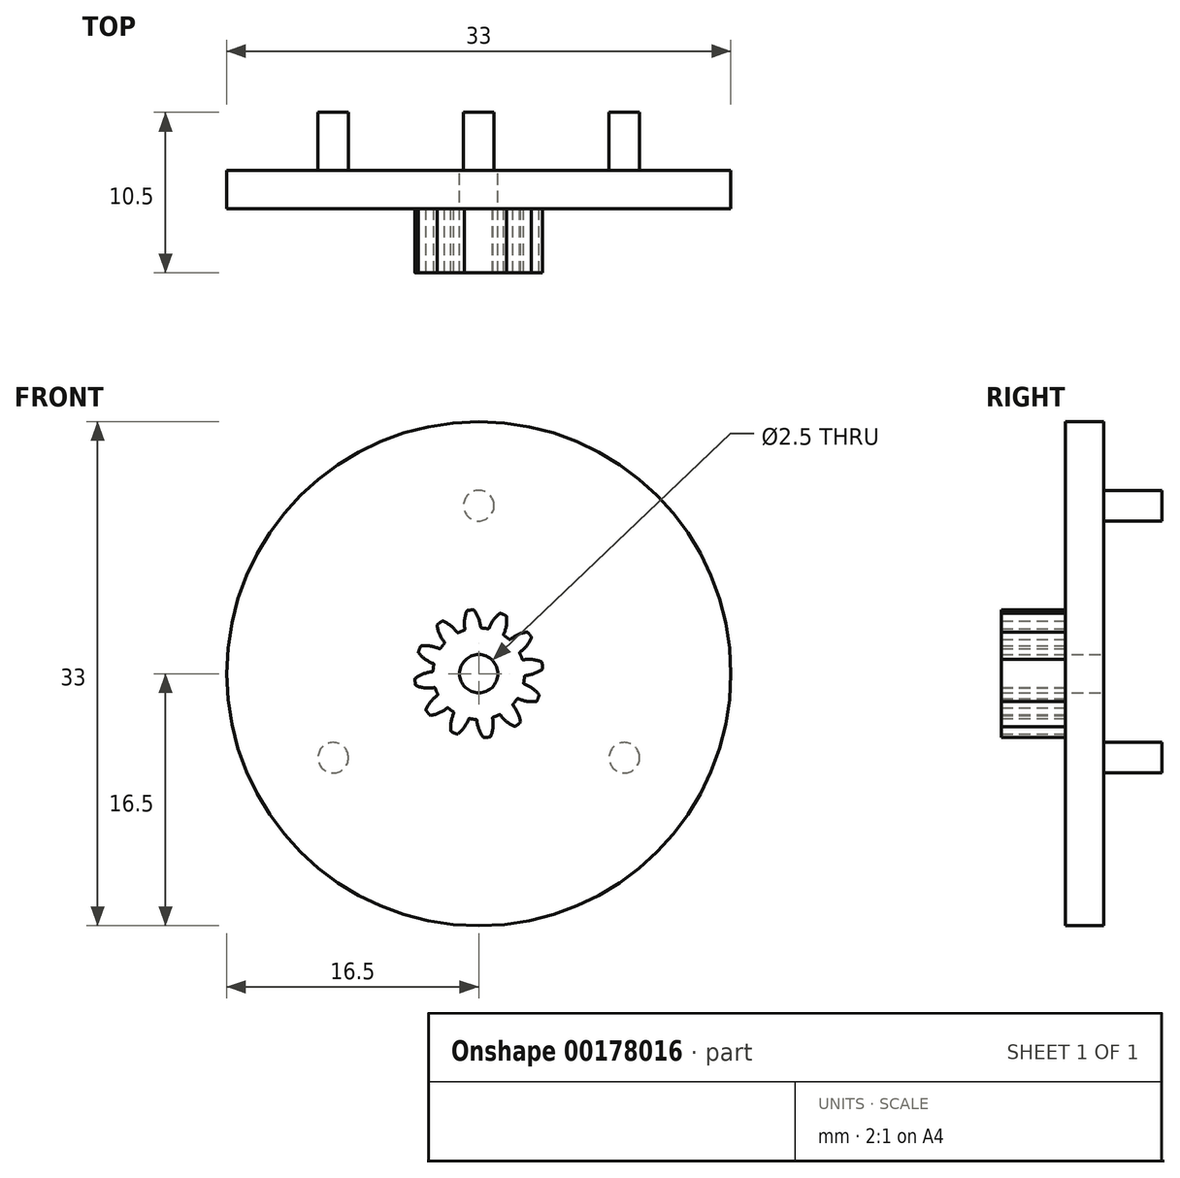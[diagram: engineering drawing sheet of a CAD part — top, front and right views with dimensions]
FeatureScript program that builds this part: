
annotation { "Feature Type Name" : "Feature", "Feature Type Description" : "" }
export const myFeature = defineFeature(function(context is Context, id is Id, definition is map)
    precondition{}
    {
        {
            var Q0;
            Q0=qCreatedBy(makeId("Front.planeOp"),FACE);
            var sketch = newSketch(context, id + "F0", { "sketchPlane" : qUnion([Q0])});
            skCircle(sketch, "E0", {"center": v(0, 0) * mm, "radius": 4.2 * mm, "construction": true});
            skCircle(sketch, "E1", {"center": v(0, 0) * mm, "radius": 3.6 * mm, "construction": true});
            skCircle(sketch, "E2", {"center": v(0, 0) * mm, "radius": 3 * mm, "construction": true});
            skLineSegment(sketch, "E3", {"start": v(0, 0) * mm, "end": v(0, 0.84) * mm, "construction": true});
            skLineSegment(sketch, "E4", {"start": v(0, 3.6) * mm, "end": v(-6.08, 3.6) * mm, "construction": true});
            skLineSegment(sketch, "E5", {"start": v(0, 3.6) * mm, "end": v(-6.1, 1.38) * mm, "construction": true});
            skCircle(sketch, "E6", {"center": v(0, 3.6) * mm, "radius": 2.16 * mm, "construction": true});
            skCircle(sketch, "E7", {"center": v(-2.03, 2.86) * mm, "radius": 2.16 * mm, "construction": true});
            skArc(sketch, "E8", {"start": v(-0.3, 4.16) * mm, "mid": v(-0.01, 3.64) * mm, "end": v(0.12, 3.06) * mm});
            skPoint(sketch, "E9.0.midPoint", {"position": v(-1.28, 0.84) * mm});
            skCircle(sketch, "E10.cCircle", {"center": v(0, 0) * mm, "radius": 0.84 * mm, "construction": true});
            skLineSegment(sketch, "E10.0", {"start": v(0, 0.84) * mm, "end": v(0.1, 0.83) * mm, "construction": true});
            skLineSegment(sketch, "E10.1", {"start": v(0.1, 0.83) * mm, "end": v(0.22, 0.8) * mm, "construction": true});
            skLineSegment(sketch, "E10.2", {"start": v(0.22, 0.8) * mm, "end": v(0.32, 0.77) * mm, "construction": true});
            skLineSegment(sketch, "E10.3", {"start": v(0.32, 0.77) * mm, "end": v(0.42, 0.72) * mm, "construction": true});
            skLineSegment(sketch, "E10.4", {"start": v(0.42, 0.72) * mm, "end": v(0.5, 0.66) * mm, "construction": true});
            skLineSegment(sketch, "E10.5", {"start": v(0.5, 0.66) * mm, "end": v(0.6, 0.6) * mm, "construction": true});
            skLineSegment(sketch, "E10.6", {"start": v(0.6, 0.6) * mm, "end": v(0.66, 0.5) * mm, "construction": true});
            skLineSegment(sketch, "E10.7", {"start": v(0.66, 0.5) * mm, "end": v(0.72, 0.42) * mm, "construction": true});
            skLineSegment(sketch, "E10.8", {"start": v(0.72, 0.42) * mm, "end": v(0.77, 0.32) * mm, "construction": true});
            skLineSegment(sketch, "E10.9", {"start": v(0.77, 0.32) * mm, "end": v(0.8, 0.22) * mm, "construction": true});
            skLineSegment(sketch, "E10.10", {"start": v(0.8, 0.22) * mm, "end": v(0.83, 0.1) * mm, "construction": true});
            skLineSegment(sketch, "E10.11", {"start": v(0.83, 0.1) * mm, "end": v(0.84, 0) * mm, "construction": true});
            skLineSegment(sketch, "E10.12", {"start": v(0.84, 0) * mm, "end": v(0.83, -0.1) * mm, "construction": true});
            skLineSegment(sketch, "E10.13", {"start": v(0.83, -0.1) * mm, "end": v(0.8, -0.22) * mm, "construction": true});
            skLineSegment(sketch, "E10.14", {"start": v(0.8, -0.22) * mm, "end": v(0.77, -0.32) * mm, "construction": true});
            skLineSegment(sketch, "E10.15", {"start": v(0.77, -0.32) * mm, "end": v(0.72, -0.42) * mm, "construction": true});
            skLineSegment(sketch, "E10.16", {"start": v(0.72, -0.42) * mm, "end": v(0.66, -0.5) * mm, "construction": true});
            skLineSegment(sketch, "E10.17", {"start": v(0.66, -0.5) * mm, "end": v(0.6, -0.6) * mm, "construction": true});
            skLineSegment(sketch, "E10.18", {"start": v(0.6, -0.6) * mm, "end": v(0.5, -0.66) * mm, "construction": true});
            skLineSegment(sketch, "E10.19", {"start": v(0.5, -0.66) * mm, "end": v(0.42, -0.72) * mm, "construction": true});
            skLineSegment(sketch, "E10.20", {"start": v(0.42, -0.72) * mm, "end": v(0.32, -0.77) * mm, "construction": true});
            skLineSegment(sketch, "E10.21", {"start": v(0.32, -0.77) * mm, "end": v(0.22, -0.8) * mm, "construction": true});
            skLineSegment(sketch, "E10.22", {"start": v(0.22, -0.8) * mm, "end": v(0.1, -0.83) * mm, "construction": true});
            skLineSegment(sketch, "E10.23", {"start": v(0.1, -0.83) * mm, "end": v(0, -0.84) * mm, "construction": true});
            skLineSegment(sketch, "E10.24", {"start": v(0, -0.84) * mm, "end": v(-0.1, -0.83) * mm, "construction": true});
            skLineSegment(sketch, "E10.25", {"start": v(-0.1, -0.83) * mm, "end": v(-0.22, -0.8) * mm, "construction": true});
            skLineSegment(sketch, "E10.26", {"start": v(-0.22, -0.8) * mm, "end": v(-0.32, -0.77) * mm, "construction": true});
            skLineSegment(sketch, "E10.27", {"start": v(-0.32, -0.77) * mm, "end": v(-0.42, -0.72) * mm, "construction": true});
            skLineSegment(sketch, "E10.28", {"start": v(-0.42, -0.72) * mm, "end": v(-0.5, -0.66) * mm, "construction": true});
            skLineSegment(sketch, "E10.29", {"start": v(-0.5, -0.66) * mm, "end": v(-0.6, -0.6) * mm, "construction": true});
            skLineSegment(sketch, "E10.30", {"start": v(-0.6, -0.6) * mm, "end": v(-0.66, -0.5) * mm, "construction": true});
            skLineSegment(sketch, "E10.31", {"start": v(-0.66, -0.5) * mm, "end": v(-0.72, -0.42) * mm, "construction": true});
            skLineSegment(sketch, "E10.32", {"start": v(-0.72, -0.42) * mm, "end": v(-0.77, -0.32) * mm, "construction": true});
            skLineSegment(sketch, "E10.33", {"start": v(-0.77, -0.32) * mm, "end": v(-0.8, -0.22) * mm, "construction": true});
            skLineSegment(sketch, "E10.34", {"start": v(-0.8, -0.22) * mm, "end": v(-0.83, -0.1) * mm, "construction": true});
            skLineSegment(sketch, "E10.35", {"start": v(-0.83, -0.1) * mm, "end": v(-0.84, 0) * mm, "construction": true});
            skLineSegment(sketch, "E10.36", {"start": v(-0.84, 0) * mm, "end": v(-0.83, 0.1) * mm, "construction": true});
            skLineSegment(sketch, "E10.37", {"start": v(-0.83, 0.1) * mm, "end": v(-0.8, 0.22) * mm, "construction": true});
            skLineSegment(sketch, "E10.38", {"start": v(-0.8, 0.22) * mm, "end": v(-0.77, 0.32) * mm, "construction": true});
            skLineSegment(sketch, "E10.39", {"start": v(-0.77, 0.32) * mm, "end": v(-0.72, 0.42) * mm, "construction": true});
            skLineSegment(sketch, "E10.40", {"start": v(-0.72, 0.42) * mm, "end": v(-0.66, 0.5) * mm, "construction": true});
            skLineSegment(sketch, "E10.41", {"start": v(-0.66, 0.5) * mm, "end": v(-0.6, 0.6) * mm, "construction": true});
            skLineSegment(sketch, "E10.42", {"start": v(-0.6, 0.6) * mm, "end": v(-0.5, 0.66) * mm, "construction": true});
            skLineSegment(sketch, "E10.43", {"start": v(-0.5, 0.66) * mm, "end": v(-0.42, 0.72) * mm, "construction": true});
            skLineSegment(sketch, "E10.44", {"start": v(-0.42, 0.72) * mm, "end": v(-0.32, 0.77) * mm, "construction": true});
            skLineSegment(sketch, "E10.45", {"start": v(-0.32, 0.77) * mm, "end": v(-0.22, 0.8) * mm, "construction": true});
            skLineSegment(sketch, "E10.46", {"start": v(-0.22, 0.8) * mm, "end": v(-0.1, 0.83) * mm, "construction": true});
            skLineSegment(sketch, "E10.47", {"start": v(-0.1, 0.83) * mm, "end": v(0, 0.84) * mm, "construction": true});
            skLineSegment(sketch, "E11", {"start": v(0, 0) * mm, "end": v(-0.1, 0.83) * mm, "construction": true});
            skArc(sketch, "E12.MirrorCS", {"start": v(-0.79, 4.1) * mm, "mid": v(-0.93, 3.52) * mm, "end": v(-0.9, 2.92) * mm});
            skArc(sketch, "E13", {"start": v(-0.73, 4.14) * mm, "mid": v(-0.55, 4.16) * mm, "end": v(-0.36, 4.18) * mm});
            skArc(sketch, "E14", {"start": v(-0.96, 2.84) * mm, "mid": v(0.4, -2.97) * mm, "end": v(0.19, 3) * mm});
            skPoint(sketch, "E15.visualSharp", {"position": v(-0.9, 2.86) * mm});
            skArc(sketch, "E15.filletArc", {"start": v(-0.96, 2.84) * mm, "mid": v(-0.92, 2.87) * mm, "end": v(-0.9, 2.92) * mm});
            skPoint(sketch, "E16.visualSharp", {"position": v(-0.77, 4.13) * mm});
            skArc(sketch, "E16.filletArc", {"start": v(-0.73, 4.14) * mm, "mid": v(-0.76, 4.12) * mm, "end": v(-0.79, 4.1) * mm});
            skPoint(sketch, "E17.visualSharp", {"position": v(-0.32, 4.19) * mm});
            skArc(sketch, "E17.filletArc", {"start": v(-0.3, 4.16) * mm, "mid": v(-0.33, 4.18) * mm, "end": v(-0.36, 4.18) * mm});
            skArc(sketch, "E18.filletArc", {"start": v(0.12, 3.06) * mm, "mid": v(0.14, 3.01) * mm, "end": v(0.19, 3) * mm});
            skArc(sketch, "E19.1.0", {"start": v(-2.25, 1.98) * mm, "mid": v(-2.23, 2.03) * mm, "end": v(-2.25, 2.08) * mm});
            skArc(sketch, "E19.1.1", {"start": v(-2.73, 3.15) * mm, "mid": v(-2.56, 2.58) * mm, "end": v(-2.25, 2.08) * mm});
            skArc(sketch, "E19.1.2", {"start": v(-2.7, 3.22) * mm, "mid": v(-2.72, 3.19) * mm, "end": v(-2.73, 3.15) * mm});
            skArc(sketch, "E19.1.3", {"start": v(-2.7, 3.22) * mm, "mid": v(-2.56, 3.33) * mm, "end": v(-2.4, 3.44) * mm});
            skArc(sketch, "E19.1.4", {"start": v(-2.34, 3.45) * mm, "mid": v(-2.37, 3.45) * mm, "end": v(-2.4, 3.44) * mm});
            skArc(sketch, "E19.1.5", {"start": v(-2.34, 3.45) * mm, "mid": v(-1.83, 3.14) * mm, "end": v(-1.42, 2.71) * mm});
            skArc(sketch, "E19.1.6", {"start": v(-1.42, 2.71) * mm, "mid": v(-1.38, 2.68) * mm, "end": v(-1.33, 2.69) * mm});
            skArc(sketch, "E19.2.0", {"start": v(-2.94, 0.6) * mm, "mid": v(-2.95, 0.64) * mm, "end": v(-2.99, 0.67) * mm});
            skArc(sketch, "E19.2.1", {"start": v(-3.94, 1.37) * mm, "mid": v(-3.5, 0.95) * mm, "end": v(-2.99, 0.67) * mm});
            skArc(sketch, "E19.2.2", {"start": v(-3.95, 1.43) * mm, "mid": v(-3.95, 1.4) * mm, "end": v(-3.94, 1.37) * mm});
            skArc(sketch, "E19.2.3", {"start": v(-3.95, 1.43) * mm, "mid": v(-3.88, 1.6) * mm, "end": v(-3.8, 1.78) * mm});
            skArc(sketch, "E19.2.4", {"start": v(-3.75, 1.82) * mm, "mid": v(-3.78, 1.8) * mm, "end": v(-3.8, 1.78) * mm});
            skArc(sketch, "E19.2.5", {"start": v(-3.75, 1.82) * mm, "mid": v(-3.16, 1.8) * mm, "end": v(-2.59, 1.63) * mm});
            skArc(sketch, "E19.2.6", {"start": v(-2.59, 1.63) * mm, "mid": v(-2.54, 1.63) * mm, "end": v(-2.5, 1.66) * mm});
            skArc(sketch, "E19.3.0", {"start": v(-2.84, -0.96) * mm, "mid": v(-2.87, -0.92) * mm, "end": v(-2.92, -0.9) * mm});
            skArc(sketch, "E19.3.1", {"start": v(-4.1, -0.79) * mm, "mid": v(-3.52, -0.93) * mm, "end": v(-2.92, -0.9) * mm});
            skArc(sketch, "E19.3.2", {"start": v(-4.14, -0.73) * mm, "mid": v(-4.12, -0.76) * mm, "end": v(-4.1, -0.79) * mm});
            skArc(sketch, "E19.3.3", {"start": v(-4.14, -0.73) * mm, "mid": v(-4.16, -0.55) * mm, "end": v(-4.18, -0.36) * mm});
            skArc(sketch, "E19.3.4", {"start": v(-4.16, -0.3) * mm, "mid": v(-4.18, -0.33) * mm, "end": v(-4.18, -0.36) * mm});
            skArc(sketch, "E19.3.5", {"start": v(-4.16, -0.3) * mm, "mid": v(-3.64, -0.01) * mm, "end": v(-3.06, 0.12) * mm});
            skArc(sketch, "E19.3.6", {"start": v(-3.06, 0.12) * mm, "mid": v(-3.01, 0.14) * mm, "end": v(-3, 0.19) * mm});
            skArc(sketch, "E19.4.0", {"start": v(-1.98, -2.25) * mm, "mid": v(-2.03, -2.23) * mm, "end": v(-2.08, -2.25) * mm});
            skArc(sketch, "E19.4.1", {"start": v(-3.15, -2.73) * mm, "mid": v(-2.58, -2.56) * mm, "end": v(-2.08, -2.25) * mm});
            skArc(sketch, "E19.4.2", {"start": v(-3.22, -2.7) * mm, "mid": v(-3.19, -2.72) * mm, "end": v(-3.15, -2.73) * mm});
            skArc(sketch, "E19.4.3", {"start": v(-3.22, -2.7) * mm, "mid": v(-3.33, -2.56) * mm, "end": v(-3.44, -2.4) * mm});
            skArc(sketch, "E19.4.4", {"start": v(-3.45, -2.34) * mm, "mid": v(-3.45, -2.37) * mm, "end": v(-3.44, -2.4) * mm});
            skArc(sketch, "E19.4.5", {"start": v(-3.45, -2.34) * mm, "mid": v(-3.14, -1.83) * mm, "end": v(-2.71, -1.42) * mm});
            skArc(sketch, "E19.4.6", {"start": v(-2.71, -1.42) * mm, "mid": v(-2.68, -1.38) * mm, "end": v(-2.69, -1.33) * mm});
            skArc(sketch, "E19.5.0", {"start": v(-0.6, -2.94) * mm, "mid": v(-0.64, -2.95) * mm, "end": v(-0.67, -2.99) * mm});
            skArc(sketch, "E19.5.1", {"start": v(-1.37, -3.94) * mm, "mid": v(-0.95, -3.5) * mm, "end": v(-0.67, -2.99) * mm});
            skArc(sketch, "E19.5.2", {"start": v(-1.43, -3.95) * mm, "mid": v(-1.4, -3.95) * mm, "end": v(-1.37, -3.94) * mm});
            skArc(sketch, "E19.5.3", {"start": v(-1.43, -3.95) * mm, "mid": v(-1.6, -3.88) * mm, "end": v(-1.78, -3.8) * mm});
            skArc(sketch, "E19.5.4", {"start": v(-1.82, -3.75) * mm, "mid": v(-1.8, -3.78) * mm, "end": v(-1.78, -3.8) * mm});
            skArc(sketch, "E19.5.5", {"start": v(-1.82, -3.75) * mm, "mid": v(-1.8, -3.16) * mm, "end": v(-1.63, -2.59) * mm});
            skArc(sketch, "E19.5.6", {"start": v(-1.63, -2.59) * mm, "mid": v(-1.63, -2.54) * mm, "end": v(-1.66, -2.5) * mm});
            skArc(sketch, "E19.6.0", {"start": v(0.96, -2.84) * mm, "mid": v(0.92, -2.87) * mm, "end": v(0.9, -2.92) * mm});
            skArc(sketch, "E19.6.1", {"start": v(0.79, -4.1) * mm, "mid": v(0.93, -3.52) * mm, "end": v(0.9, -2.92) * mm});
            skArc(sketch, "E19.6.2", {"start": v(0.73, -4.14) * mm, "mid": v(0.76, -4.12) * mm, "end": v(0.79, -4.1) * mm});
            skArc(sketch, "E19.6.3", {"start": v(0.73, -4.14) * mm, "mid": v(0.55, -4.16) * mm, "end": v(0.36, -4.18) * mm});
            skArc(sketch, "E19.6.4", {"start": v(0.3, -4.16) * mm, "mid": v(0.33, -4.18) * mm, "end": v(0.36, -4.18) * mm});
            skArc(sketch, "E19.6.5", {"start": v(0.3, -4.16) * mm, "mid": v(0.01, -3.64) * mm, "end": v(-0.12, -3.06) * mm});
            skArc(sketch, "E19.6.6", {"start": v(-0.12, -3.06) * mm, "mid": v(-0.14, -3.01) * mm, "end": v(-0.19, -3) * mm});
            skArc(sketch, "E19.7.0", {"start": v(2.25, -1.98) * mm, "mid": v(2.23, -2.03) * mm, "end": v(2.25, -2.08) * mm});
            skArc(sketch, "E19.7.1", {"start": v(2.73, -3.15) * mm, "mid": v(2.56, -2.58) * mm, "end": v(2.25, -2.08) * mm});
            skArc(sketch, "E19.7.2", {"start": v(2.7, -3.22) * mm, "mid": v(2.72, -3.19) * mm, "end": v(2.73, -3.15) * mm});
            skArc(sketch, "E19.7.3", {"start": v(2.7, -3.22) * mm, "mid": v(2.56, -3.33) * mm, "end": v(2.4, -3.44) * mm});
            skArc(sketch, "E19.7.4", {"start": v(2.34, -3.45) * mm, "mid": v(2.37, -3.45) * mm, "end": v(2.4, -3.44) * mm});
            skArc(sketch, "E19.7.5", {"start": v(2.34, -3.45) * mm, "mid": v(1.83, -3.14) * mm, "end": v(1.42, -2.71) * mm});
            skArc(sketch, "E19.7.6", {"start": v(1.42, -2.71) * mm, "mid": v(1.38, -2.68) * mm, "end": v(1.33, -2.69) * mm});
            skArc(sketch, "E19.8.0", {"start": v(2.94, -0.6) * mm, "mid": v(2.95, -0.64) * mm, "end": v(2.99, -0.67) * mm});
            skArc(sketch, "E19.8.1", {"start": v(3.94, -1.37) * mm, "mid": v(3.5, -0.95) * mm, "end": v(2.99, -0.67) * mm});
            skArc(sketch, "E19.8.2", {"start": v(3.95, -1.43) * mm, "mid": v(3.95, -1.4) * mm, "end": v(3.94, -1.37) * mm});
            skArc(sketch, "E19.8.3", {"start": v(3.95, -1.43) * mm, "mid": v(3.88, -1.6) * mm, "end": v(3.8, -1.78) * mm});
            skArc(sketch, "E19.8.4", {"start": v(3.75, -1.82) * mm, "mid": v(3.78, -1.8) * mm, "end": v(3.8, -1.78) * mm});
            skArc(sketch, "E19.8.5", {"start": v(3.75, -1.82) * mm, "mid": v(3.16, -1.8) * mm, "end": v(2.59, -1.63) * mm});
            skArc(sketch, "E19.8.6", {"start": v(2.59, -1.63) * mm, "mid": v(2.54, -1.63) * mm, "end": v(2.5, -1.66) * mm});
            skArc(sketch, "E19.9.0", {"start": v(2.84, 0.96) * mm, "mid": v(2.87, 0.92) * mm, "end": v(2.92, 0.9) * mm});
            skArc(sketch, "E19.9.1", {"start": v(4.1, 0.79) * mm, "mid": v(3.52, 0.93) * mm, "end": v(2.92, 0.9) * mm});
            skArc(sketch, "E19.9.2", {"start": v(4.14, 0.73) * mm, "mid": v(4.12, 0.76) * mm, "end": v(4.1, 0.79) * mm});
            skArc(sketch, "E19.9.3", {"start": v(4.14, 0.73) * mm, "mid": v(4.16, 0.55) * mm, "end": v(4.18, 0.36) * mm});
            skArc(sketch, "E19.9.4", {"start": v(4.16, 0.3) * mm, "mid": v(4.18, 0.33) * mm, "end": v(4.18, 0.36) * mm});
            skArc(sketch, "E19.9.5", {"start": v(4.16, 0.3) * mm, "mid": v(3.64, 0.01) * mm, "end": v(3.06, -0.12) * mm});
            skArc(sketch, "E19.9.6", {"start": v(3.06, -0.12) * mm, "mid": v(3.01, -0.14) * mm, "end": v(3, -0.19) * mm});
            skArc(sketch, "E19.10.0", {"start": v(1.98, 2.25) * mm, "mid": v(2.03, 2.23) * mm, "end": v(2.08, 2.25) * mm});
            skArc(sketch, "E19.10.1", {"start": v(3.15, 2.73) * mm, "mid": v(2.58, 2.56) * mm, "end": v(2.08, 2.25) * mm});
            skArc(sketch, "E19.10.2", {"start": v(3.22, 2.7) * mm, "mid": v(3.19, 2.72) * mm, "end": v(3.15, 2.73) * mm});
            skArc(sketch, "E19.10.3", {"start": v(3.22, 2.7) * mm, "mid": v(3.33, 2.56) * mm, "end": v(3.44, 2.4) * mm});
            skArc(sketch, "E19.10.4", {"start": v(3.45, 2.34) * mm, "mid": v(3.45, 2.37) * mm, "end": v(3.44, 2.4) * mm});
            skArc(sketch, "E19.10.5", {"start": v(3.45, 2.34) * mm, "mid": v(3.14, 1.83) * mm, "end": v(2.71, 1.42) * mm});
            skArc(sketch, "E19.10.6", {"start": v(2.71, 1.42) * mm, "mid": v(2.68, 1.38) * mm, "end": v(2.69, 1.33) * mm});
            skArc(sketch, "E19.11.0", {"start": v(0.6, 2.94) * mm, "mid": v(0.64, 2.95) * mm, "end": v(0.67, 2.99) * mm});
            skArc(sketch, "E19.11.1", {"start": v(1.37, 3.94) * mm, "mid": v(0.95, 3.5) * mm, "end": v(0.67, 2.99) * mm});
            skArc(sketch, "E19.11.2", {"start": v(1.43, 3.95) * mm, "mid": v(1.4, 3.95) * mm, "end": v(1.37, 3.94) * mm});
            skArc(sketch, "E19.11.3", {"start": v(1.43, 3.95) * mm, "mid": v(1.6, 3.88) * mm, "end": v(1.78, 3.8) * mm});
            skArc(sketch, "E19.11.4", {"start": v(1.82, 3.75) * mm, "mid": v(1.8, 3.78) * mm, "end": v(1.78, 3.8) * mm});
            skArc(sketch, "E19.11.5", {"start": v(1.82, 3.75) * mm, "mid": v(1.8, 3.16) * mm, "end": v(1.63, 2.59) * mm});
            skArc(sketch, "E19.11.6", {"start": v(1.63, 2.59) * mm, "mid": v(1.63, 2.54) * mm, "end": v(1.66, 2.5) * mm});
            skSolve(sketch);
        }
        {
            var Q0;
            Q0=qSketchRegion(id+"F0",true);
            extrude(context, id + "F1", {"entities" : qUnion([Q0]), "depth" : 4.2 * mm});
        }
        {
            var Q0;
            Q0=makeQuery(id+"F1.opExtrude","CAP_FACE",FACE,{"disambiguationData":[OSD([sQuery(id+"F0.wireOp",EDGE,"E8"),sQuery(id+"F0.wireOp",EDGE,"E12.MirrorCS"),sQuery(id+"F0.wireOp",EDGE,"E13"),sQuery(id+"F0.wireOp",EDGE,"E14"),sQuery(id+"F0.wireOp",EDGE,"E15.filletArc"),sQuery(id+"F0.wireOp",EDGE,"E16.filletArc"),sQuery(id+"F0.wireOp",EDGE,"E17.filletArc"),sQuery(id+"F0.wireOp",EDGE,"E18.filletArc"),sQuery(id+"F0.wireOp",EDGE,"E19.1.0"),sQuery(id+"F0.wireOp",EDGE,"E19.1.1"),sQuery(id+"F0.wireOp",EDGE,"E19.1.2"),sQuery(id+"F0.wireOp",EDGE,"E19.1.3"),sQuery(id+"F0.wireOp",EDGE,"E19.1.4"),sQuery(id+"F0.wireOp",EDGE,"E19.1.5"),sQuery(id+"F0.wireOp",EDGE,"E19.1.6"),sQuery(id+"F0.wireOp",EDGE,"E19.2.0"),sQuery(id+"F0.wireOp",EDGE,"E19.2.1"),sQuery(id+"F0.wireOp",EDGE,"E19.2.2"),sQuery(id+"F0.wireOp",EDGE,"E19.2.3"),sQuery(id+"F0.wireOp",EDGE,"E19.2.4"),sQuery(id+"F0.wireOp",EDGE,"E19.2.5"),sQuery(id+"F0.wireOp",EDGE,"E19.2.6"),sQuery(id+"F0.wireOp",EDGE,"E19.3.0"),sQuery(id+"F0.wireOp",EDGE,"E19.3.1"),sQuery(id+"F0.wireOp",EDGE,"E19.3.2"),sQuery(id+"F0.wireOp",EDGE,"E19.3.3"),sQuery(id+"F0.wireOp",EDGE,"E19.3.4"),sQuery(id+"F0.wireOp",EDGE,"E19.3.5"),sQuery(id+"F0.wireOp",EDGE,"E19.3.6"),sQuery(id+"F0.wireOp",EDGE,"E19.4.0"),sQuery(id+"F0.wireOp",EDGE,"E19.4.1"),sQuery(id+"F0.wireOp",EDGE,"E19.4.2"),sQuery(id+"F0.wireOp",EDGE,"E19.4.3"),sQuery(id+"F0.wireOp",EDGE,"E19.4.4"),sQuery(id+"F0.wireOp",EDGE,"E19.4.5"),sQuery(id+"F0.wireOp",EDGE,"E19.4.6"),sQuery(id+"F0.wireOp",EDGE,"E19.5.0"),sQuery(id+"F0.wireOp",EDGE,"E19.5.1"),sQuery(id+"F0.wireOp",EDGE,"E19.5.2"),sQuery(id+"F0.wireOp",EDGE,"E19.5.3"),sQuery(id+"F0.wireOp",EDGE,"E19.5.4"),sQuery(id+"F0.wireOp",EDGE,"E19.5.5"),sQuery(id+"F0.wireOp",EDGE,"E19.5.6"),sQuery(id+"F0.wireOp",EDGE,"E19.6.0"),sQuery(id+"F0.wireOp",EDGE,"E19.6.1"),sQuery(id+"F0.wireOp",EDGE,"E19.6.2"),sQuery(id+"F0.wireOp",EDGE,"E19.6.3"),sQuery(id+"F0.wireOp",EDGE,"E19.6.4"),sQuery(id+"F0.wireOp",EDGE,"E19.6.5"),sQuery(id+"F0.wireOp",EDGE,"E19.6.6"),sQuery(id+"F0.wireOp",EDGE,"E19.7.0"),sQuery(id+"F0.wireOp",EDGE,"E19.7.1"),sQuery(id+"F0.wireOp",EDGE,"E19.7.2"),sQuery(id+"F0.wireOp",EDGE,"E19.7.3"),sQuery(id+"F0.wireOp",EDGE,"E19.7.4"),sQuery(id+"F0.wireOp",EDGE,"E19.7.5"),sQuery(id+"F0.wireOp",EDGE,"E19.7.6"),sQuery(id+"F0.wireOp",EDGE,"E19.8.0"),sQuery(id+"F0.wireOp",EDGE,"E19.8.1"),sQuery(id+"F0.wireOp",EDGE,"E19.8.2"),sQuery(id+"F0.wireOp",EDGE,"E19.8.3"),sQuery(id+"F0.wireOp",EDGE,"E19.8.4"),sQuery(id+"F0.wireOp",EDGE,"E19.8.5"),sQuery(id+"F0.wireOp",EDGE,"E19.8.6"),sQuery(id+"F0.wireOp",EDGE,"E19.9.0"),sQuery(id+"F0.wireOp",EDGE,"E19.9.1"),sQuery(id+"F0.wireOp",EDGE,"E19.9.2"),sQuery(id+"F0.wireOp",EDGE,"E19.9.3"),sQuery(id+"F0.wireOp",EDGE,"E19.9.4"),sQuery(id+"F0.wireOp",EDGE,"E19.9.5"),sQuery(id+"F0.wireOp",EDGE,"E19.9.6"),sQuery(id+"F0.wireOp",EDGE,"E19.10.0"),sQuery(id+"F0.wireOp",EDGE,"E19.10.1"),sQuery(id+"F0.wireOp",EDGE,"E19.10.2"),sQuery(id+"F0.wireOp",EDGE,"E19.10.3"),sQuery(id+"F0.wireOp",EDGE,"E19.10.4"),sQuery(id+"F0.wireOp",EDGE,"E19.10.5"),sQuery(id+"F0.wireOp",EDGE,"E19.10.6"),sQuery(id+"F0.wireOp",EDGE,"E19.11.0"),sQuery(id+"F0.wireOp",EDGE,"E19.11.1"),sQuery(id+"F0.wireOp",EDGE,"E19.11.2"),sQuery(id+"F0.wireOp",EDGE,"E19.11.3"),sQuery(id+"F0.wireOp",EDGE,"E19.11.4"),sQuery(id+"F0.wireOp",EDGE,"E19.11.5"),sQuery(id+"F0.wireOp",EDGE,"E19.11.6")])],"isStart":true});
            var sketch = newSketch(context, id + "F2", { "sketchPlane" : qUnion([Q0])});
            skCircle(sketch, "E20", {"center": v(0, 0) * mm, "radius": 16.5 * mm});
            skSolve(sketch);
        }
        {
            var Q0;
            Q0=qSketchRegion(id+"F2",true);
            extrude(context, id + "F3", {"entities" : qUnion([Q0]), "operationType" : NewBodyOperationType.ADD, "depth" : 2.5 * mm});
        }
        {
            var Q0;
            Q0=makeQuery(id+"F3.opExtrude","CAP_FACE",FACE,{"disambiguationData":[OSD([sQuery(id+"F2.wireOp",EDGE,"E20")])],"isStart":false});
            var sketch = newSketch(context, id + "F4", { "sketchPlane" : qUnion([Q0])});
            skLineSegment(sketch, "E21", {"start": v(0, 0) * mm, "end": v(0, 5.49) * mm, "construction": true});
            skCircle(sketch, "E22", {"center": v(0, 11) * mm, "radius": 1 * mm});
            skCircle(sketch, "E23.1.0", {"center": v(-9.53, -5.5) * mm, "radius": 1 * mm});
            skCircle(sketch, "E23.2.0", {"center": v(9.53, -5.5) * mm, "radius": 1 * mm});
            skPoint(sketch, "E23.center", {"position": v(0, 0) * mm});
            skSolve(sketch);
        }
        {
            var Q0;
            Q0=qSketchRegion(id+"F4",true);
            extrude(context, id + "F5", {"entities" : qUnion([Q0]), "operationType" : NewBodyOperationType.ADD, "depth" : 3.8 * mm});
        }
        {
            var Q0;
            Q0=makeQuery(id+"F1.opExtrude","CAP_FACE",FACE,{"disambiguationData":[OSD([sQuery(id+"F0.wireOp",EDGE,"E8"),sQuery(id+"F0.wireOp",EDGE,"E12.MirrorCS"),sQuery(id+"F0.wireOp",EDGE,"E13"),sQuery(id+"F0.wireOp",EDGE,"E14"),sQuery(id+"F0.wireOp",EDGE,"E15.filletArc"),sQuery(id+"F0.wireOp",EDGE,"E16.filletArc"),sQuery(id+"F0.wireOp",EDGE,"E17.filletArc"),sQuery(id+"F0.wireOp",EDGE,"E18.filletArc"),sQuery(id+"F0.wireOp",EDGE,"E19.1.0"),sQuery(id+"F0.wireOp",EDGE,"E19.1.1"),sQuery(id+"F0.wireOp",EDGE,"E19.1.2"),sQuery(id+"F0.wireOp",EDGE,"E19.1.3"),sQuery(id+"F0.wireOp",EDGE,"E19.1.4"),sQuery(id+"F0.wireOp",EDGE,"E19.1.5"),sQuery(id+"F0.wireOp",EDGE,"E19.1.6"),sQuery(id+"F0.wireOp",EDGE,"E19.2.0"),sQuery(id+"F0.wireOp",EDGE,"E19.2.1"),sQuery(id+"F0.wireOp",EDGE,"E19.2.2"),sQuery(id+"F0.wireOp",EDGE,"E19.2.3"),sQuery(id+"F0.wireOp",EDGE,"E19.2.4"),sQuery(id+"F0.wireOp",EDGE,"E19.2.5"),sQuery(id+"F0.wireOp",EDGE,"E19.2.6"),sQuery(id+"F0.wireOp",EDGE,"E19.3.0"),sQuery(id+"F0.wireOp",EDGE,"E19.3.1"),sQuery(id+"F0.wireOp",EDGE,"E19.3.2"),sQuery(id+"F0.wireOp",EDGE,"E19.3.3"),sQuery(id+"F0.wireOp",EDGE,"E19.3.4"),sQuery(id+"F0.wireOp",EDGE,"E19.3.5"),sQuery(id+"F0.wireOp",EDGE,"E19.3.6"),sQuery(id+"F0.wireOp",EDGE,"E19.4.0"),sQuery(id+"F0.wireOp",EDGE,"E19.4.1"),sQuery(id+"F0.wireOp",EDGE,"E19.4.2"),sQuery(id+"F0.wireOp",EDGE,"E19.4.3"),sQuery(id+"F0.wireOp",EDGE,"E19.4.4"),sQuery(id+"F0.wireOp",EDGE,"E19.4.5"),sQuery(id+"F0.wireOp",EDGE,"E19.4.6"),sQuery(id+"F0.wireOp",EDGE,"E19.5.0"),sQuery(id+"F0.wireOp",EDGE,"E19.5.1"),sQuery(id+"F0.wireOp",EDGE,"E19.5.2"),sQuery(id+"F0.wireOp",EDGE,"E19.5.3"),sQuery(id+"F0.wireOp",EDGE,"E19.5.4"),sQuery(id+"F0.wireOp",EDGE,"E19.5.5"),sQuery(id+"F0.wireOp",EDGE,"E19.5.6"),sQuery(id+"F0.wireOp",EDGE,"E19.6.0"),sQuery(id+"F0.wireOp",EDGE,"E19.6.1"),sQuery(id+"F0.wireOp",EDGE,"E19.6.2"),sQuery(id+"F0.wireOp",EDGE,"E19.6.3"),sQuery(id+"F0.wireOp",EDGE,"E19.6.4"),sQuery(id+"F0.wireOp",EDGE,"E19.6.5"),sQuery(id+"F0.wireOp",EDGE,"E19.6.6"),sQuery(id+"F0.wireOp",EDGE,"E19.7.0"),sQuery(id+"F0.wireOp",EDGE,"E19.7.1"),sQuery(id+"F0.wireOp",EDGE,"E19.7.2"),sQuery(id+"F0.wireOp",EDGE,"E19.7.3"),sQuery(id+"F0.wireOp",EDGE,"E19.7.4"),sQuery(id+"F0.wireOp",EDGE,"E19.7.5"),sQuery(id+"F0.wireOp",EDGE,"E19.7.6"),sQuery(id+"F0.wireOp",EDGE,"E19.8.0"),sQuery(id+"F0.wireOp",EDGE,"E19.8.1"),sQuery(id+"F0.wireOp",EDGE,"E19.8.2"),sQuery(id+"F0.wireOp",EDGE,"E19.8.3"),sQuery(id+"F0.wireOp",EDGE,"E19.8.4"),sQuery(id+"F0.wireOp",EDGE,"E19.8.5"),sQuery(id+"F0.wireOp",EDGE,"E19.8.6"),sQuery(id+"F0.wireOp",EDGE,"E19.9.0"),sQuery(id+"F0.wireOp",EDGE,"E19.9.1"),sQuery(id+"F0.wireOp",EDGE,"E19.9.2"),sQuery(id+"F0.wireOp",EDGE,"E19.9.3"),sQuery(id+"F0.wireOp",EDGE,"E19.9.4"),sQuery(id+"F0.wireOp",EDGE,"E19.9.5"),sQuery(id+"F0.wireOp",EDGE,"E19.9.6"),sQuery(id+"F0.wireOp",EDGE,"E19.10.0"),sQuery(id+"F0.wireOp",EDGE,"E19.10.1"),sQuery(id+"F0.wireOp",EDGE,"E19.10.2"),sQuery(id+"F0.wireOp",EDGE,"E19.10.3"),sQuery(id+"F0.wireOp",EDGE,"E19.10.4"),sQuery(id+"F0.wireOp",EDGE,"E19.10.5"),sQuery(id+"F0.wireOp",EDGE,"E19.10.6"),sQuery(id+"F0.wireOp",EDGE,"E19.11.0"),sQuery(id+"F0.wireOp",EDGE,"E19.11.1"),sQuery(id+"F0.wireOp",EDGE,"E19.11.2"),sQuery(id+"F0.wireOp",EDGE,"E19.11.3"),sQuery(id+"F0.wireOp",EDGE,"E19.11.4"),sQuery(id+"F0.wireOp",EDGE,"E19.11.5"),sQuery(id+"F0.wireOp",EDGE,"E19.11.6")])],"isStart":false});
            var sketch = newSketch(context, id + "F6", { "sketchPlane" : qUnion([Q0])});
            skCircle(sketch, "E24", {"center": v(0, 0) * mm, "radius": 1.25 * mm});
            skSolve(sketch);
        }
        {
            var Q0;
            Q0=qSketchRegion(id+"F6",true);
            extrude(context, id + "F7", {"entities" : qUnion([Q0]), "operationType" : NewBodyOperationType.REMOVE, "depth" : 25 * mm, "hasSecondDirection" : true, "secondDirectionOppositeDirection" : true, "secondDirectionDepth" : 25 * mm});
        }
    });
